# Revit family: BIMLIB_ПланкаОколооконнаяСложная_GRANDLINE
name_source: partatom
category: Обобщенные модели
revit_build: Autodesk Revit 2017 (Build: 20170118_1100(x64)
units: mm (PartAtom-declared; Revit-internal decimal feet)

## family parameters
Может служить основой для арматурных стержней = Нет
Общий = Нет
При загрузке вырезать с полостями = Нет
Размер круглого соединителя = Использовать диаметр
Тип детали = Нормальный
Точка расчета площади = Нет

## types (4) — shared parameters
ADSK_URL документации изделия = https://www.grandline.ru
ADSK_URL страницы изделия = https://www.grandline.ru
ADSK_Версия Revit = 2017
ADSK_Группирование = Доборные элементы
ADSK_Единица измерения = м
ADSK_Завод-изготовитель = Grand Line
ADSK_Материал = GL_Drap_RAL7016
ADSK_Материал тип подсчета = 1
ADSK_Обозначение = ГОСТ 19904-90, ГОСТ 14918-80
BL_BIM library = https://bimlib.pro
URL = https://www.grandline.ru
Изготовитель = Grand Line

## per-type parameters (varying)
| type | ADSK_Код изделия | ADSK_Наименование | Описание | Профиль_Высота | Профиль_Глубина |
| 200х75 | M12.102.006 | Околооконная планка сложная 200х75 | Околооконная планка сложная 200х75 | 75 мм | 200 мм |
| 200х50 | M12.102.005 | Околооконная планка сложная 200х50 | Околооконная планка сложная 200х50 | 50 мм | 200 мм |
| 250х50 | M12.102.007 | Околооконная планка сложная 250х50 | Околооконная планка сложная 250х50 | 50 мм | 250 мм |
| 250х75 | M12.102.008 | Околооконная планка сложная 250х75 | Околооконная планка сложная 250х75 | 75 мм | 250 мм |
